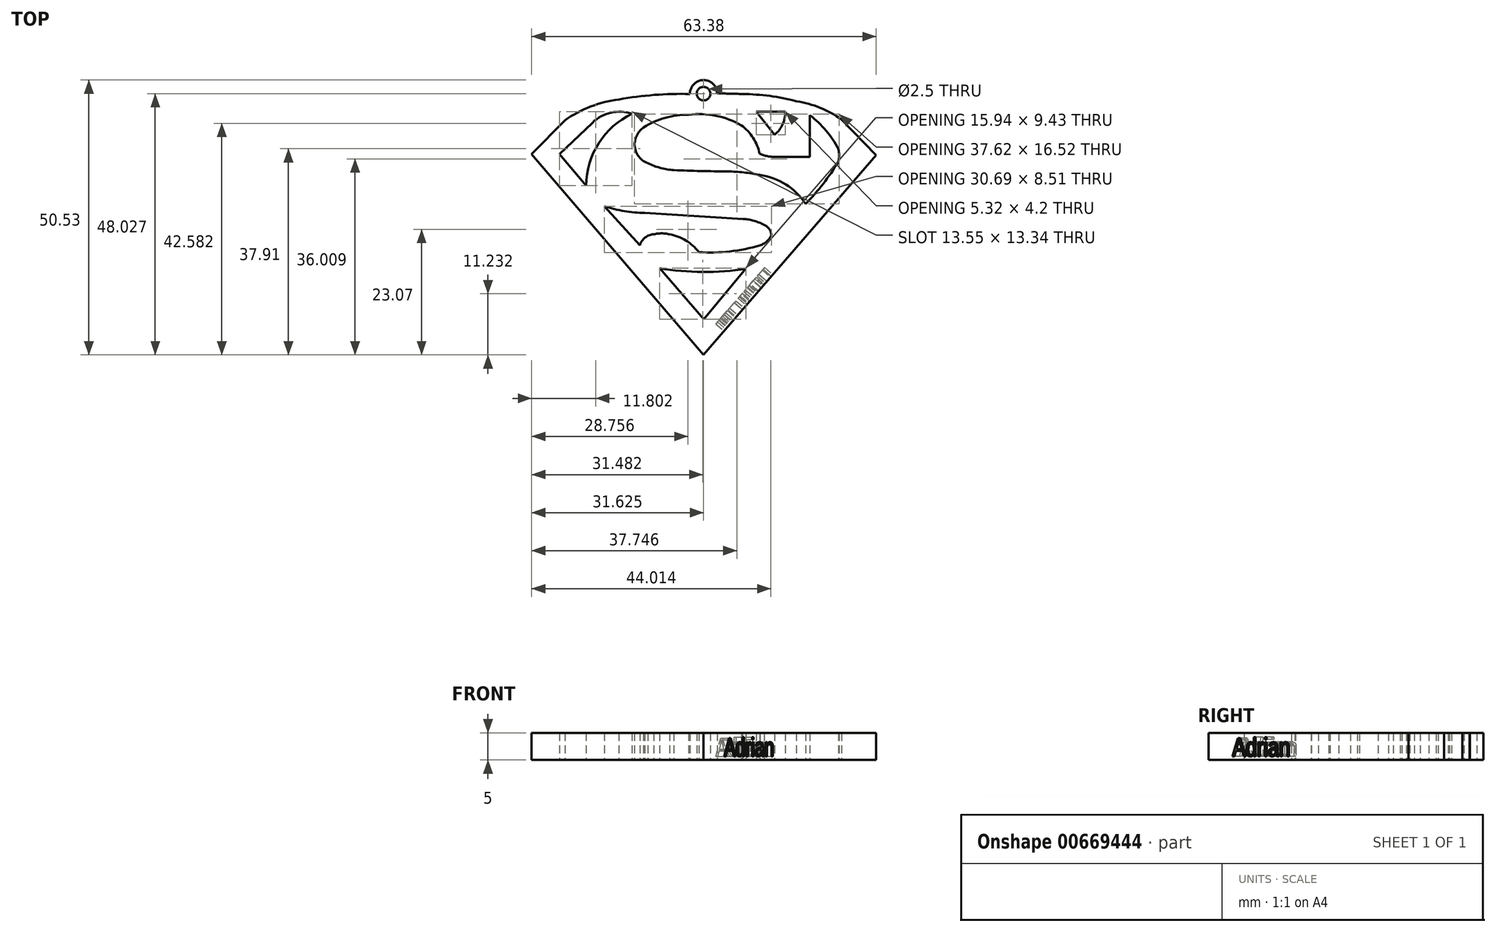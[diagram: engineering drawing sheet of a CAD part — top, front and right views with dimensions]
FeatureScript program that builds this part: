
annotation { "Feature Type Name" : "Feature", "Feature Type Description" : "" }
export const myFeature = defineFeature(function(context is Context, id is Id, definition is map)
    precondition{}
    {
        {
            var Q0;
            Q0=qCreatedBy(makeId("Top.planeOp"),FACE);
            var sketch = newSketch(context, id + "F0", { "sketchPlane" : qUnion([Q0])});
            skLineSegment(sketch, "E0", {"start": v(100, 0) * mm, "end": v(-100, 0) * mm, "construction": true});
            skLineSegment(sketch, "E1", {"start": v(0, 100) * mm, "end": v(0, -100) * mm, "construction": true});
            skLineSegment(sketch, "E2", {"start": v(24.78, 16.86) * mm, "end": v(32.94, 7.43) * mm});
            skLineSegment(sketch, "E3", {"start": v(32.94, 7.43) * mm, "end": v(40.72, 16.76) * mm});
            skArc(sketch, "E4", {"start": v(24.78, 16.86) * mm, "mid": v(32.75, 16.14) * mm, "end": v(40.72, 16.76) * mm});
            skLineSegment(sketch, "E5", {"start": v(11.3, 32.05) * mm, "end": v(6.4, 37.8) * mm});
            skLineSegment(sketch, "E6", {"start": v(6.4, 37.8) * mm, "end": v(12.47, 43.62) * mm});
            skArc(sketch, "E7", {"start": v(19.74, 45.21) * mm, "mid": v(13.62, 39.85) * mm, "end": v(11.3, 32.05) * mm});
            skArc(sketch, "E8", {"start": v(19.74, 45.21) * mm, "mid": v(15.88, 45.44) * mm, "end": v(12.47, 43.62) * mm});
            skLineSegment(sketch, "E9", {"start": v(52.45, 44.96) * mm, "end": v(52.45, 37.28) * mm});
            skLineSegment(sketch, "E10", {"start": v(52.45, 37.28) * mm, "end": v(46.22, 37.28) * mm});
            skLineSegment(sketch, "E11", {"start": v(42.62, 45.6) * mm, "end": v(47.95, 45.6) * mm});
            skLineSegment(sketch, "E12", {"start": v(42.62, 45.6) * mm, "end": v(45.98, 41.4) * mm});
            skArc(sketch, "E13", {"start": v(45.98, 41.4) * mm, "mid": v(47.44, 43.27) * mm, "end": v(47.95, 45.6) * mm});
            skArc(sketch, "E14", {"start": v(43.23, 37.88) * mm, "mid": v(44.7, 37.43) * mm, "end": v(46.22, 37.28) * mm});
            skArc(sketch, "E15", {"start": v(57.69, 38.74) * mm, "mid": v(55.43, 42.15) * mm, "end": v(52.45, 44.96) * mm});
            skArc(sketch, "E16", {"start": v(57.69, 36.41) * mm, "mid": v(57.83, 37.58) * mm, "end": v(57.69, 38.74) * mm});
            skArc(sketch, "E17", {"start": v(51.67, 28.66) * mm, "mid": v(48.03, 32.24) * mm, "end": v(43.23, 33.98) * mm});
            skArc(sketch, "E18", {"start": v(51.67, 28.66) * mm, "mid": v(54.9, 32.36) * mm, "end": v(57.69, 36.41) * mm});
            skArc(sketch, "E19", {"start": v(43.23, 37.88) * mm, "mid": v(42.02, 40.8) * mm, "end": v(39.87, 43.11) * mm});
            skArc(sketch, "E20", {"start": v(39.87, 43.11) * mm, "mid": v(35.17, 44.88) * mm, "end": v(30.16, 45.08) * mm});
            skArc(sketch, "E21", {"start": v(30.16, 45.08) * mm, "mid": v(25.84, 44.5) * mm, "end": v(21.84, 42.73) * mm});
            skArc(sketch, "E22", {"start": v(21.84, 42.73) * mm, "mid": v(20.73, 41.43) * mm, "end": v(20.2, 39.8) * mm});
            skArc(sketch, "E23", {"start": v(20.2, 39.8) * mm, "mid": v(20.82, 37.58) * mm, "end": v(22.63, 36.14) * mm});
            skArc(sketch, "E24", {"start": v(22.63, 36.14) * mm, "mid": v(24.96, 35.29) * mm, "end": v(27.4, 34.87) * mm});
            skArc(sketch, "E25", {"start": v(27.4, 34.87) * mm, "mid": v(32.36, 34.71) * mm, "end": v(37.32, 34.63) * mm});
            skArc(sketch, "E26", {"start": v(43.23, 33.98) * mm, "mid": v(40.3, 34.45) * mm, "end": v(37.32, 34.63) * mm});
            skLineSegment(sketch, "E27", {"start": v(14.68, 28.23) * mm, "end": v(21.2, 21.06) * mm});
            skArc(sketch, "E28", {"start": v(23.73, 23.07) * mm, "mid": v(22.14, 22.48) * mm, "end": v(21.2, 21.06) * mm});
            skArc(sketch, "E29", {"start": v(26.65, 23.07) * mm, "mid": v(25.19, 23.25) * mm, "end": v(23.73, 23.07) * mm});
            skArc(sketch, "E30", {"start": v(32.02, 19.79) * mm, "mid": v(29.64, 21.94) * mm, "end": v(26.65, 23.07) * mm});
            skArc(sketch, "E31", {"start": v(32.02, 19.79) * mm, "mid": v(37.72, 19.92) * mm, "end": v(43.31, 21.06) * mm});
            skArc(sketch, "E32", {"start": v(43.31, 21.06) * mm, "mid": v(44.56, 21.79) * mm, "end": v(45.37, 22.97) * mm});
            skArc(sketch, "E33", {"start": v(14.68, 28.23) * mm, "mid": v(18.35, 27.34) * mm, "end": v(22.1, 26.99) * mm});
            skLineSegment(sketch, "E34", {"start": v(22.1, 26.99) * mm, "end": v(40.19, 25.9) * mm});
            skArc(sketch, "E35", {"start": v(44.03, 24.82) * mm, "mid": v(42.16, 25.56) * mm, "end": v(40.19, 25.9) * mm});
            skArc(sketch, "E36", {"start": v(45.37, 22.97) * mm, "mid": v(44.95, 24.08) * mm, "end": v(44.03, 24.82) * mm});
            skLineSegment(sketch, "E37", {"start": v(1.27, 37.79) * mm, "end": v(32.9, 0.9) * mm});
            skLineSegment(sketch, "E38", {"start": v(32.9, 0.9) * mm, "end": v(64.65, 37.64) * mm});
            skLineSegment(sketch, "E39", {"start": v(64.65, 37.64) * mm, "end": v(58.29, 44.17) * mm});
            skLineSegment(sketch, "E40", {"start": v(1.27, 37.79) * mm, "end": v(7.4, 44.06) * mm});
            skArc(sketch, "E41", {"start": v(17.34, 47.87) * mm, "mid": v(12.14, 46.56) * mm, "end": v(7.4, 44.06) * mm});
            skArc(sketch, "E42", {"start": v(30.69, 48.86) * mm, "mid": v(23.99, 48.72) * mm, "end": v(17.34, 47.87) * mm});
            skArc(sketch, "E43", {"start": v(40.07, 48.86) * mm, "mid": v(35.38, 48.97) * mm, "end": v(30.69, 48.86) * mm});
            skArc(sketch, "E44", {"start": v(49.96, 47.55) * mm, "mid": v(45.05, 48.51) * mm, "end": v(40.07, 48.86) * mm});
            skArc(sketch, "E45", {"start": v(58.29, 44.17) * mm, "mid": v(54.32, 46.35) * mm, "end": v(49.96, 47.55) * mm});
            skLineSegment(sketch, "E46", {"start": v(32.9, 0.9) * mm, "end": v(32.9, 50) * mm, "construction": true});
            skCircle(sketch, "E47", {"center": v(32.9, 48.94) * mm, "radius": 2.5 * mm});
            skCircle(sketch, "E48", {"center": v(32.9, 48.94) * mm, "radius": 1.25 * mm});
            skSolve(sketch);
        }
        {
            var Q0;
            Q0 = qSketchRegion(id + "F0", true);
            extrude(context, id + "F1", {"entities" : qUnion([Q0]), "depth" : 5 * mm, "offsetDistance" : 25 * mm});
        }
        {
            var Q0;
            Q0=makeQuery(id+"F1.opExtrude","SWEPT_FACE",FACE,{"disambiguationData":[OSD([sQuery(id+"F0.wireOp",EDGE,"E38")])]});
            var sketch = newSketch(context, id + "F2", { "sketchPlane" : qUnion([Q0])});
            skText(sketch, "E49", { "text": "Adrian", "fontName": "Arimo-Regular.ttf"});
            const initialGuessF2  = {"E49": [0.02796, 0.00068, 1, 0, 0.0035]};
            skSetInitialGuess(sketch, initialGuessF2);
            skSolve(sketch);
        }
        {
            var Q0;
            Q0 = qSketchRegion(id + "F2", true);
            extrude(context, id + "F3", {"entities" : qUnion([Q0]), "operationType" : NewBodyOperationType.REMOVE, "oppositeDirection" : true, "depth" : 2 * mm, "offsetDistance" : 25 * mm});
        }
    });
